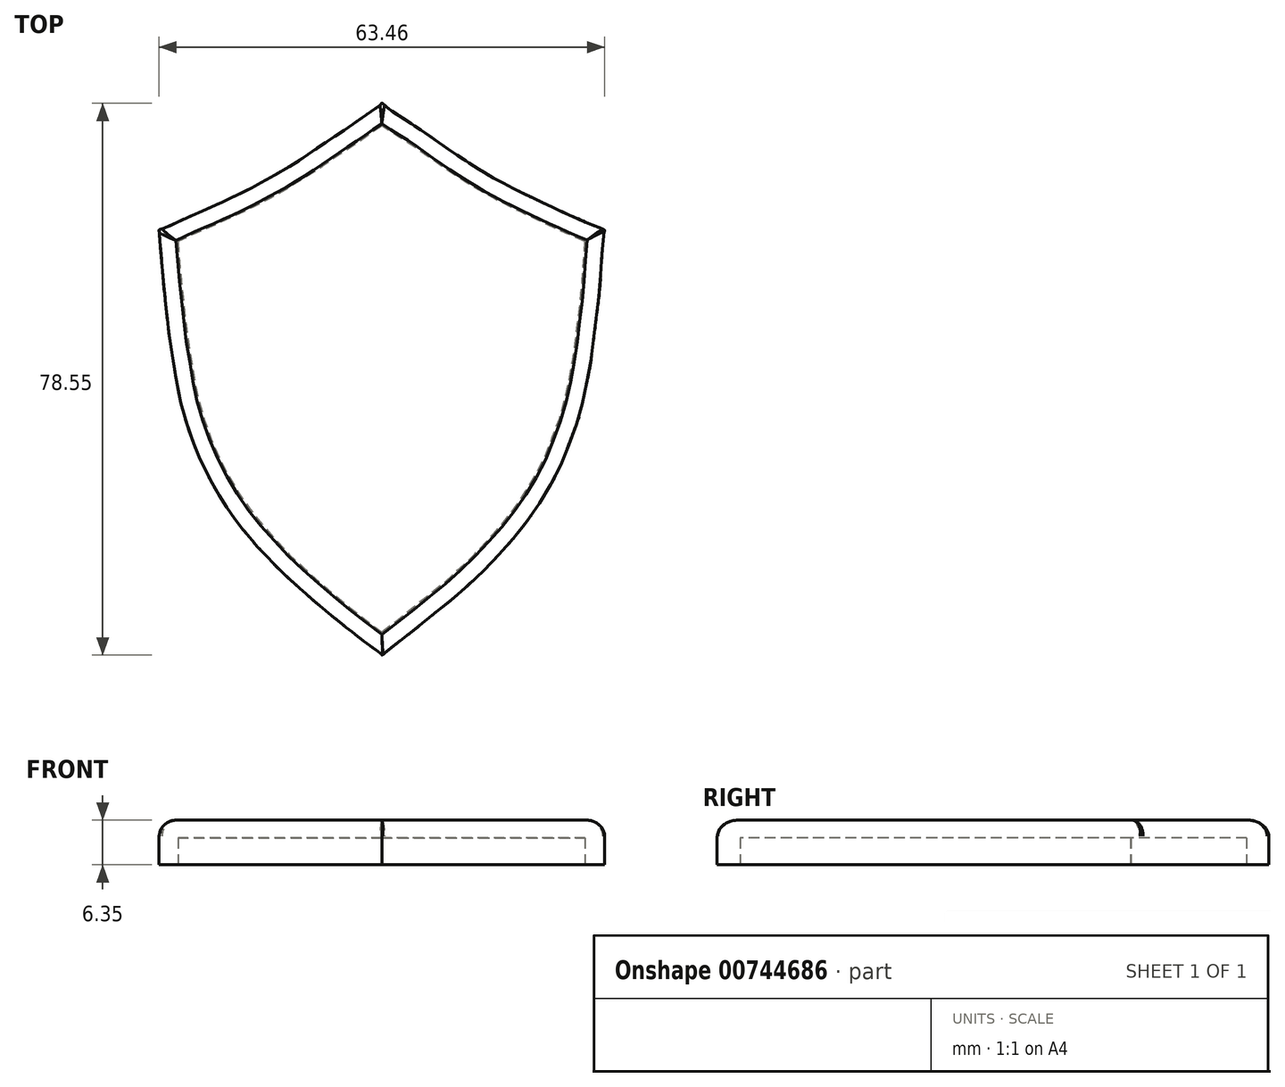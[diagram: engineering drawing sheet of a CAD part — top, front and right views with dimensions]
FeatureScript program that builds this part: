
annotation { "Feature Type Name" : "Feature", "Feature Type Description" : "" }
export const myFeature = defineFeature(function(context is Context, id is Id, definition is map)
    precondition{}
    {
        {
            var Q0;
            Q0=qCreatedBy(makeId("Top.planeOp"),FACE);
            var sketch = newSketch(context, id + "F0", { "sketchPlane" : qUnion([Q0])});
            skFitSpline(sketch, "E0", {"points": [v(-18.42, -22.98) * mm, v(-18.09, -23.42) * mm, v(-17.6, -23.94) * mm, v(-17.17, -24.36) * mm, v(-16.58, -25.01) * mm, v(-15.77, -25.84) * mm, v(-14.92, -26.76) * mm, v(-10.58, -30.73) * mm, v(-9.46, -31.7) * mm, v(-7.03, -33.72) * mm, v(-1.32, -38.17) * mm, v(0, -39.2) * mm, v(0, -39.24) * mm, v(1.07, -38.37) * mm, v(2, -37.66) * mm, v(2.98, -36.9) * mm, v(5.17, -35.17) * mm, v(8.53, -32.45) * mm, v(9.2, -31.95) * mm, v(14.77, -26.92) * mm, v(16.78, -24.76) * mm, v(17.69, -23.8) * mm, v(18.5, -22.86) * mm, v(19.22, -22) * mm, v(20.63, -20.2) * mm, v(21.24, -19.35) * mm, v(23.27, -16.27) * mm, v(24.45, -14.2) * mm, v(26.09, -10.76) * mm, v(26.29, -10.17) * mm, v(27.1, -7.91) * mm, v(28.15, -4.96) * mm, v(29, -1.16) * mm, v(29.68, 2.21) * mm, v(30.23, 6.57) * mm, v(30.93, 12.23) * mm, v(31.2, 15.89) * mm, v(31.67, 21.08) * mm, v(31.72, 21.22) * mm, v(29.58, 22.14) * mm, v(21.94, 25.62) * mm, v(17.33, 27.9) * mm, v(13.6, 30.05) * mm, v(9.45, 32.8) * mm, v(4.55, 36.18) * mm, v(0.52, 38.9) * mm, v(0, 39.31) * mm, v(-0.29, 39.04) * mm, v(-1.69, 38.06) * mm, v(-4.73, 35.93) * mm, v(-8.34, 33.52) * mm, v(-10.25, 32.2) * mm, v(-14.04, 29.8) * mm, v(-17.79, 27.68) * mm, v(-22.9, 25.18) * mm, v(-26.88, 23.41) * mm, v(-29.56, 22.2) * mm, v(-31.3, 21.43) * mm, v(-31.7, 21.31) * mm, v(-31.7, 20.96) * mm, v(-31.63, 20.18) * mm, v(-31.16, 14.38) * mm, v(-30.73, 10.25) * mm, v(-30.32, 6.65) * mm, v(-29.77, 3) * mm, v(-29.15, -0.79) * mm, v(-28.6, -3.43) * mm, v(-27.3, -7.71) * mm, v(-25.6, -11.92) * mm, v(-23.66, -15.68) * mm, v(-21.55, -18.98) * mm, v(-19.66, -21.5) * mm, v(-18.42, -22.98) * mm]});
            skSolve(sketch);
        }
        {
            var Q0;
            Q0=qSketchRegion(id+"F0",true);
            extrude(context, id + "F1", {"entities" : qUnion([Q0]), "depth" : 6.35 * mm});
        }
        {
            var Q0;
            Q0=makeQuery(id+"F1.opExtrude","CAP_EDGE",EDGE,{"disambiguationData":[OSD([sQuery(id+"F0.wireOp",EDGE,"E0")])],"isStart":false});
            fillet(context, id + "F2", {"entities" : qUnion([Q0]), "radius" : 2.3 * mm, "tangentPropagation" : true, "allowEdgeOverflow" : false});
        }
        {
            var Q0;
            Q0=makeQuery(id+"F1.opExtrude","CAP_FACE",FACE,{"disambiguationData":[OSD([sQuery(id+"F0.wireOp",EDGE,"E0")])],"isStart":true});
            shell(context, id + "F3", {"entities" : qUnion([Q0]), "thickness" : 2.54 * mm});
        }
    });
